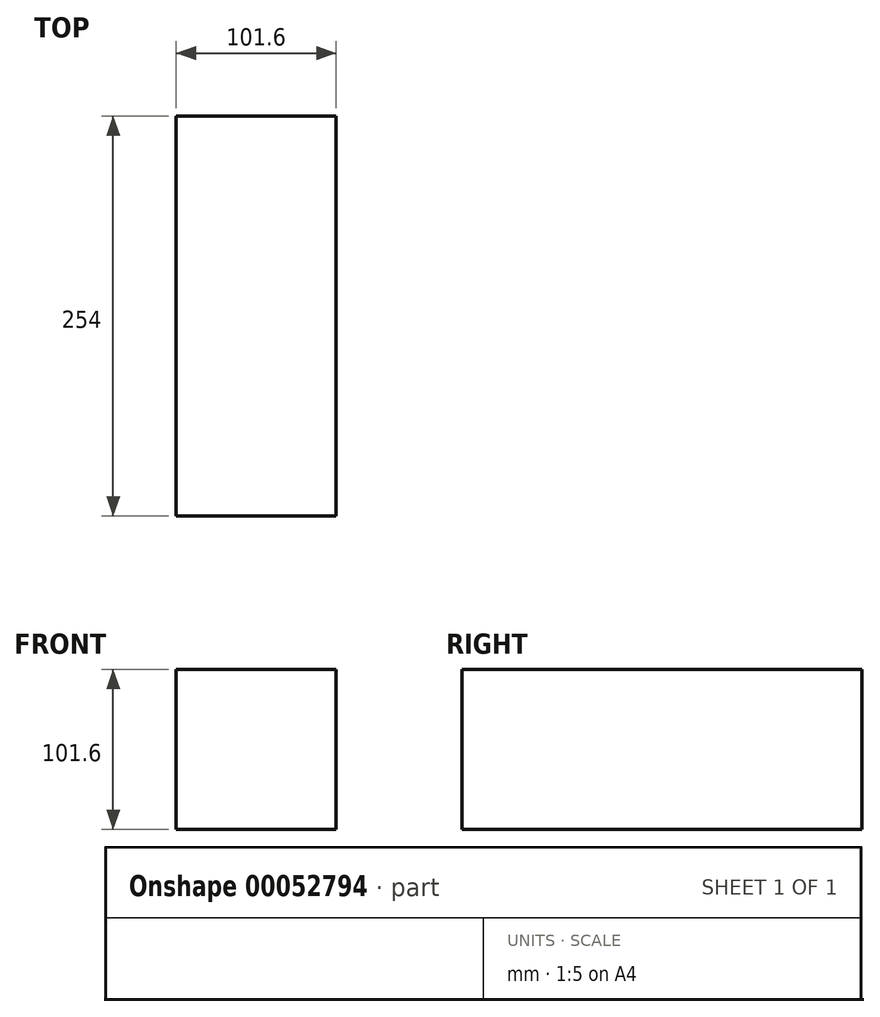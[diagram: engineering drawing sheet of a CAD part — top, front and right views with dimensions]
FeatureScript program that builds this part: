
annotation { "Feature Type Name" : "Feature", "Feature Type Description" : "" }
export const myFeature = defineFeature(function(context is Context, id is Id, definition is map)
    precondition{}
    {
        {
            var Q0;
            Q0=qCreatedBy(makeId("Front.planeOp"),FACE);
            var sketch = newSketch(context, id + "F0", { "sketchPlane" : qUnion([Q0])});
            skLineSegment(sketch, "E0", {"start": v(-53.23, 64.52) * mm, "end": v(-53.23, -37.08) * mm});
            skLineSegment(sketch, "E1", {"start": v(48.37, -37.08) * mm, "end": v(-53.23, -37.08) * mm});
            skLineSegment(sketch, "E2", {"start": v(-53.23, 64.52) * mm, "end": v(48.37, 64.52) * mm});
            skLineSegment(sketch, "E3", {"start": v(48.37, 64.52) * mm, "end": v(48.37, -37.08) * mm});
            skSolve(sketch);
        }
        {
            var Q0;
            Q0=makeQuery(id+"F0.imprint","IMPRINT",FACE,{"disambiguationData":[TD([[makeQuery(id+"F0.imprint","IMPRINT",EDGE,{"derivedFrom":sQuery(id+"F0.wireOp",EDGE,"E0")}),1.0]])]});
            extrude(context, id + "F1", {"entities" : qUnion([Q0]), "depth" : 254 * mm});
        }
    });
